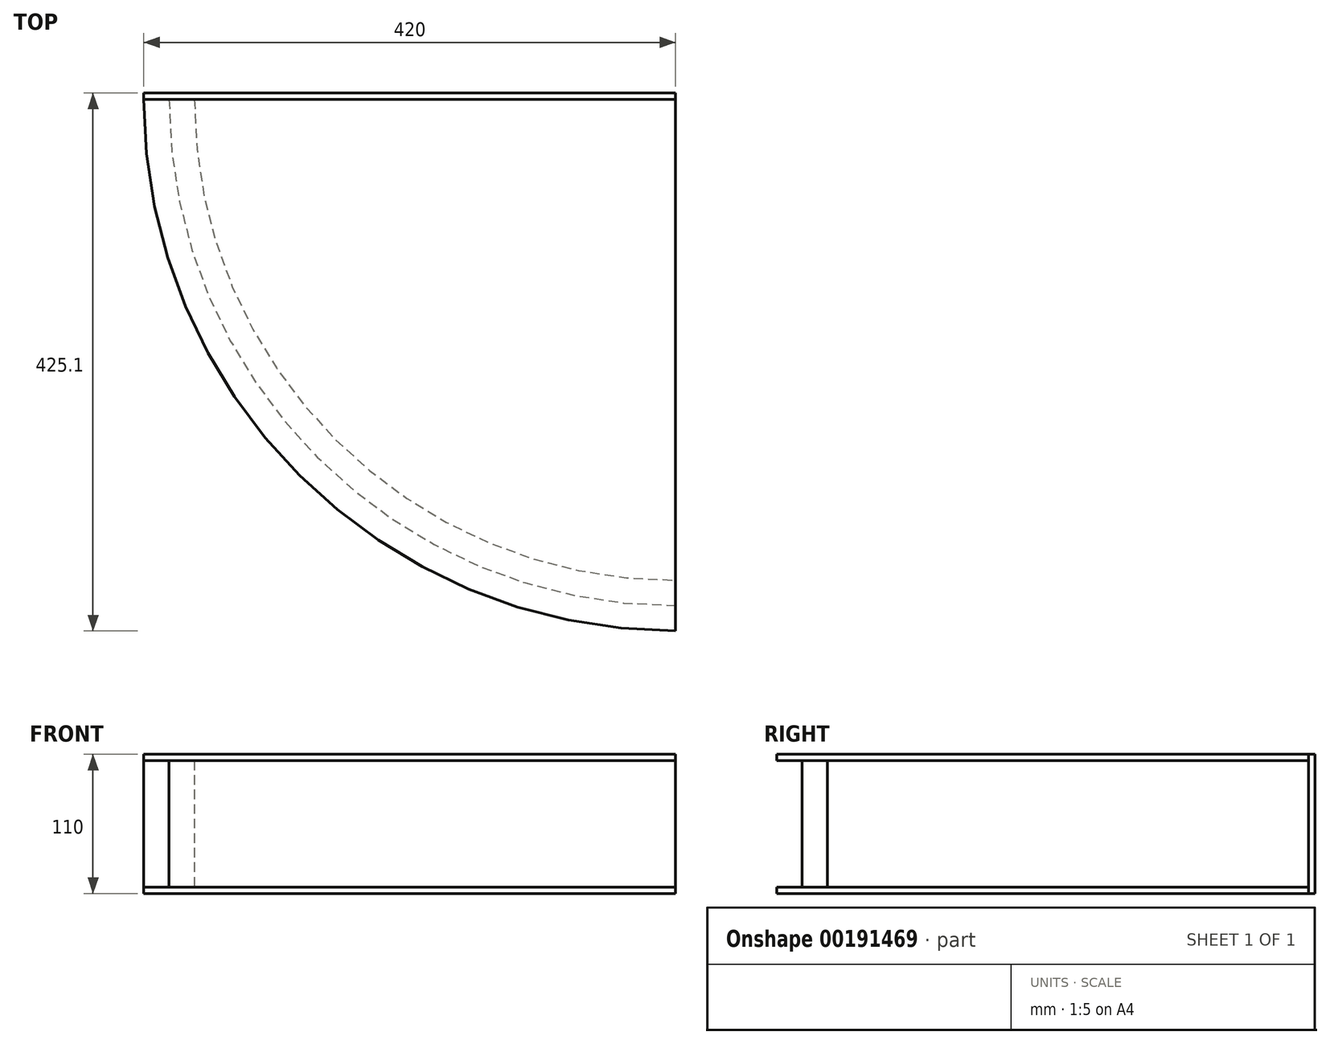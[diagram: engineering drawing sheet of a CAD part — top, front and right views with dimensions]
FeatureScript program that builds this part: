
annotation { "Feature Type Name" : "Feature", "Feature Type Description" : "" }
export const myFeature = defineFeature(function(context is Context, id is Id, definition is map)
    precondition{}
    {
        {
            var Q0;
            Q0=qCreatedBy(makeId("Top.planeOp"),FACE);
            var sketch = newSketch(context, id + "F0", { "sketchPlane" : qUnion([Q0])});
            skLineSegment(sketch, "E0", {"start": v(0, 0) * mm, "end": v(-400, 0) * mm});
            skArc(sketch, "E1", {"start": v(-400, 0) * mm, "mid": v(-282.84, -282.84) * mm, "end": v(0, -400) * mm});
            skLineSegment(sketch, "E2", {"start": v(0, 0) * mm, "end": v(0, -400) * mm});
            skArc(sketch, "E3.0", {"start": v(-380, 0) * mm, "mid": v(-268.7, -268.7) * mm, "end": v(0, -380) * mm});
            skSolve(sketch);
        }
        {
            var Q0;
            {var subQ0=sQuery(id+"F0.wireOp",EDGE,"E1");Q0=makeQuery(id+"F0.imprint","IMPRINT",FACE,{"disambiguationData":[TD([[makeQuery(id+"F0.imprint","IMPRINT",EDGE,{"derivedFrom":subQ0}),1.0]])]});}
            extrude(context, id + "F1", {"entities" : qUnion([Q0]), "depth" : 100 * mm});
        }
        {
            var Q0;
            Q0=makeQuery(id+"F1.opExtrude","CAP_FACE",FACE,{"disambiguationData":[OSD([sQuery(id+"F0.wireOp",EDGE,"E0"),sQuery(id+"F0.wireOp",EDGE,"E1"),sQuery(id+"F0.wireOp",EDGE,"E2"),sQuery(id+"F0.wireOp",EDGE,"E3.0")])],"isStart":true});
            cPlane(context, id + "F2", {"entities" : qUnion([Q0]), "cplaneType" : CPlaneType.OFFSET, "offset" : 0 * mm, "width" : 150 * mm, "height" : 150 * mm});
        }
        {
            var Q0;
            Q0=qCreatedBy(id+"F2.planeOp",FACE);
            var sketch = newSketch(context, id + "F3", { "sketchPlane" : qUnion([Q0])});
            skLineSegment(sketch, "E4", {"start": v(0, 0) * mm, "end": v(0, 420) * mm});
            skLineSegment(sketch, "E5", {"start": v(0, 0) * mm, "end": v(-420, 0) * mm});
            skArc(sketch, "E6", {"start": v(0, 400) * mm, "mid": v(-282.84, 282.84) * mm, "end": v(-400, 0) * mm});
            skArc(sketch, "E7.0", {"start": v(0, 420) * mm, "mid": v(-296.98, 296.98) * mm, "end": v(-420, 0) * mm});
            skSolve(sketch);
        }
        {
            var Q0;
            Q0 = qSketchRegion(id + "F3", true);
            extrude(context, id + "F4", {"entities" : qUnion([Q0]), "depth" : 5 * mm});
        }
        {
            var Q0;
            Q0=makeQuery(id+"F1.opExtrude","CAP_FACE",FACE,{"disambiguationData":[OSD([sQuery(id+"F0.wireOp",EDGE,"E0"),sQuery(id+"F0.wireOp",EDGE,"E1"),sQuery(id+"F0.wireOp",EDGE,"E2"),sQuery(id+"F0.wireOp",EDGE,"E3.0")])],"isStart":false});
            cPlane(context, id + "F5", {"entities" : qUnion([Q0]), "cplaneType" : CPlaneType.OFFSET, "offset" : 0 * mm, "width" : 150 * mm, "height" : 150 * mm});
        }
        {
            var Q0;
            Q0=qCreatedBy(id+"F5.planeOp",FACE);
            var sketch = newSketch(context, id + "F6", { "sketchPlane" : qUnion([Q0])});
            skLineSegment(sketch, "E8", {"start": v(0, 0) * mm, "end": v(0, -420) * mm});
            skLineSegment(sketch, "E9", {"start": v(0, 0) * mm, "end": v(-420, 0) * mm});
            skArc(sketch, "E10.0", {"start": v(-420, 0) * mm, "mid": v(-296.98, -296.98) * mm, "end": v(0, -420) * mm});
            skSolve(sketch);
        }
        {
            var Q0;
            Q0 = qSketchRegion(id + "F6", true);
            extrude(context, id + "F7", {"entities" : qUnion([Q0]), "depth" : 5 * mm});
        }
        {
            var Q0;
            Q0=makeQuery(id+"F1.opExtrude","SWEPT_FACE",FACE,{"disambiguationData":[OSD([sQuery(id+"F0.wireOp",EDGE,"E0")])]});
            cPlane(context, id + "F8", {"entities" : qUnion([Q0]), "cplaneType" : CPlaneType.OFFSET, "offset" : 0 * mm, "width" : 150 * mm, "height" : 150 * mm});
        }
        {
            var Q0;
            Q0=qCreatedBy(id+"F8.planeOp",FACE);
            var sketch = newSketch(context, id + "F9", { "sketchPlane" : qUnion([Q0])});
            skLineSegment(sketch, "E11", {"start": v(0, -5) * mm, "end": v(0, 105) * mm});
            skLineSegment(sketch, "E12", {"start": v(0, -5) * mm, "end": v(420, -5) * mm});
            skLineSegment(sketch, "E13", {"start": v(420, -5) * mm, "end": v(420, 105) * mm});
            skLineSegment(sketch, "E14", {"start": v(420, 105) * mm, "end": v(0, 105) * mm});
            skSolve(sketch);
        }
        {
            var Q0;
            Q0 = qSketchRegion(id + "F9", true);
            extrude(context, id + "F10", {"entities" : qUnion([Q0]), "depth" : 5.1 * mm});
        }
    });
